# Revit family: Class-II-Fan_VBBB-CCW-TAD_Carnes
name_source: partatom
category: Mechanical Equipment
revit_build: Autodesk Revit Architecture 2012 (Build: 20110309_2315(x64)
units: mm (PartAtom-declared; Revit-internal decimal feet)

## types (12) — shared parameters
04 CSI = 23 34 23
95 CSI = 15830
Angle = 135.00°
Assembly Code = D3040200
Catalog URL = http://www.carnes.com
Description = Cetrifugal Blowers
Housing = Aluminum-Carnes-Spun-Brushed
IOM Instructions URL = http://www.carnes.com
Manufacturer = Carnes Company
Manufacturer Fax = 608-845-6470
Motor Cover = No
Product Page URL = http://www.carnes.com
URL = http://www.carnes.com
Warranty URL = http://www.carnes.com
Weather Cover = Yes
ecoScorecard Product Page = http://ecoscorecard.com
zero-valued in all types: Default Elevation

## per-type parameters (varying)
- VBBB-CCW-TAD 12: 001=21.6 "; A=13 "; B=9.8 "; C=13.3 "; D=17.6 "; DX=1 "; Drip=4.9 "; Drip1=4.9 "; G=16 "; H=32 "; HA=9.8 "; HC=13.9 "; HE=10.6 "; HG=9.3 "; HJ=9.3 "; HN=12.9 "; J=7.4 "; KL=2 "; Model=VBBB 12; Motor Pedastal Stand=18.6 "; P=26.5 "; Radius=6.6 "; SD=1.2 "; SD Radius=0.6 "; SE=2.8 "; Support Plate Drip=17.6 "; Weather Cover Height=22.4 "; Weather Cover Length=23.4 "; Weather Cover Width=13 "
- VBBB-CCW-TAD 13: 001=24.2 "; A=14.3 "; B=10.8 "; C=14.6 "; D=19.1 "; DX=1 "; Drip=7.4 "; Drip1=5.4 "; G=17.5 "; H=34.8 "; HA=10.8 "; HC=15.3 "; HE=11.6 "; HG=10.3 "; HJ=10.3 "; HN=14.3 "; J=8 "; KL=2.6 "; Model=VBBB 13; Motor Pedastal Stand=20.5 "; P=29.6 "; Radius=7.3 "; SD=1.2 "; SD Radius=0.6 "; SE=3.4 "; Support Plate Drip=15.8 "; Weather Cover Height=22.8 "; Weather Cover Length=25.4 "; Weather Cover Width=14.5 "
- VBBB-CCW-TAD 15: 001=24.2 "; A=15.9 "; B=11.9 "; C=16.2 "; D=19.4 "; DX=1 "; Drip=6.9 "; Drip1=6 "; G=19 "; H=36 "; HA=11.9 "; HC=16.8 "; HE=12.9 "; HG=11.4 "; HJ=11.4 "; HN=15.8 "; J=9.1 "; KL=2.6 "; Model=VBBB 15; Motor Pedastal Stand=20.5 "; P=30.1 "; Radius=8.1 "; SD=1.2 "; SD Radius=0.6 "; SE=3.4 "; Support Plate Drip=17.8 "; Weather Cover Height=25.5 "; Weather Cover Length=25.4 "; Weather Cover Width=16 "
- VBBB-CCW-TAD 16: 001=24.2 "; A=17.4 "; B=13.2 "; C=17.8 "; D=19.4 "; DX=1 "; Drip=6.9 "; Drip1=6.6 "; G=20.5 "; H=37.3 "; HA=13.1 "; HC=18.4 "; HE=14.1 "; HG=12.5 "; HJ=12.6 "; HN=17.4 "; J=9.7 "; KL=2.6 "; Model=VBBB 16; Motor Pedastal Stand=20.5 "; P=30.8 "; Radius=8.9 "; SD=1.2 "; SD Radius=0.6 "; SE=3.4 "; Support Plate Drip=19 "; Weather Cover Height=28 "; Weather Cover Length=25.4 "; Weather Cover Width=17.5 "
- VBBB-CCW-TAD 18: 001=29.5 "; A=19.4 "; B=14.6 "; C=19.5 "; D=21.9 "; DX=1.3 "; Drip=6.4 "; Drip1=7.3 "; G=22.5 "; H=43.4 "; HA=14.5 "; HC=20.6 "; HE=15.7 "; HG=13.8 "; HJ=14 "; HN=19.3 "; J=10.9 "; KL=3.3 "; Model=VBBB 18; Motor Pedastal Stand=25.3 "; P=36.8 "; Radius=9.8 "; SD=1.4 "; SD Radius=0.7 "; SE=4 "; Support Plate Drip=21 "; Weather Cover Height=32 "; Weather Cover Length=30.9 "; Weather Cover Width=19.5 "
- VBBB-CCW-TAD 20: 001=29.5 "; A=21.2 "; B=15.9 "; C=21.4 "; D=22.8 "; DX=1.3 "; Drip=6.4 "; Drip1=8 "; G=25 "; H=44.8 "; HA=15.8 "; HC=22.4 "; HE=17.3 "; HG=15.2 "; HJ=15.3 "; HN=21.1 "; J=11.6 "; KL=3.3 "; Model=VBBB 20; Motor Pedastal Stand=25.3 "; P=37.5 "; Radius=10.7 "; SD=1.4 "; SD Radius=0.7 "; SE=4 "; Support Plate Drip=22.8 "; Weather Cover Height=35 "; Weather Cover Length=30.9 "; Weather Cover Width=22 "
- VBBB-CCW-TAD 22: 001=29.5 "; A=23.6 "; B=17.7 "; C=23.8 "; D=25.5 "; DX=1.3 "; Drip=6.4 "; Drip1=8.8 "; G=27.3 "; H=47.1 "; HA=17.7 "; HC=24.8 "; HE=19.1 "; HG=16.8 "; HJ=17.2 "; HN=23.5 "; J=12.4 "; KL=3.3 "; Model=VBBB 22; Motor Pedastal Stand=25.3 "; P=38.4 "; Radius=11.9 "; SD=1.4 "; SD Radius=0.7 "; SE=4 "; Support Plate Drip=25.5 "; Weather Cover Height=32.3 "; Weather Cover Length=30.8 "; Weather Cover Width=24.3 "
- VBBB-CCW-TAD 24: 001=29.5 "; A=25.9 "; B=19.4 "; C=26.1 "; D=28 "; DX=1.3 "; Drip=6.4 "; Drip1=9.7 "; G=29.8 "; H=48.8 "; HA=19.5 "; HC=27.1 "; HE=21 "; HG=18.5 "; HJ=19 "; HN=25.9 "; J=13.3 "; KL=3.3 "; Model=VBBB 24; Motor Pedastal Stand=25.3 "; P=39.3 "; Radius=13 "; SD=1.7 "; SD Radius=0.8 "; SE=4 "; Support Plate Drip=28 "; Weather Cover Height=36.4 "; Weather Cover Length=30.8 "; Weather Cover Width=26.8 "
- VBBB-CCW-TAD 27: 001=32.4 "; A=28.6 "; B=21.4 "; C=28.5 "; D=30.5 "; DX=1.5 "; Drip=6.4 "; Drip1=10.7 "; G=33 "; H=53 "; HA=21.4 "; HC=30.1 "; HE=23.2 "; HG=20.4 "; HJ=20.9 "; HN=28.6 "; J=14.3 "; KL=3.6 "; Model=VBBB 27; Motor Pedastal Stand=27.6 "; P=43.1 "; Radius=14.3 "; SD=1.7 "; SD Radius=0.8 "; SE=4.6 "; Support Plate Drip=30.5 "; Weather Cover Height=40.8 "; Weather Cover Length=33.7 "; Weather Cover Width=30 "
- VBBB-CCW-TAD 30: 001=32.5 "; A=31.8 "; B=23.8 "; C=31.6 "; D=27.5 "; DX=1.5 "; Drip=6.4 "; Drip1=11.9 "; G=36.1 "; H=56 "; HA=23.8 "; HC=33.3 "; HE=25.8 "; HG=22.8 "; HJ=23.3 "; HN=31.8 "; J=15.5 "; KL=3.6 "; Model=VBBB 30; Motor Pedastal Stand=27.7 "; P=44.4 "; Radius=15.8 "; SD=1.9 "; SD Radius=1 "; SE=4.6 "; Support Plate Drip=27.5 "; Weather Cover Height=38 "; Weather Cover Length=33.8 "; Weather Cover Width=33.1 "
- VBBB-CCW-TAD 33: 001=36.7 "; A=35.1 "; B=26.1 "; C=34.8 "; D=30 "; DX=1.5 "; Drip=6.4 "; Drip1=13 "; G=38.9 "; H=61.8 "; HA=26.3 "; HC=36.6 "; HE=28.4 "; HG=25 "; HJ=25.8 "; HN=35.1 "; J=16.6 "; KL=4.5 "; Model=VBBB 33; Motor Pedastal Stand=31.2 "; P=49.7 "; Radius=17.4 "; SD=2.2 "; SD Radius=1.1 "; SE=5.3 "; Support Plate Drip=30 "; Weather Cover Height=40.5 "; Weather Cover Length=37.9 "; Weather Cover Width=35.9 "
- VBBB-CCW-TAD 36: 001=36.6 "; A=38.8 "; B=28.9 "; C=38.5 "; D=33.5 "; DX=1.5 "; Drip=6.5 "; Drip1=14.4 "; G=43.8 "; H=64.6 "; HA=29 "; HC=40.1 "; HE=31.5 "; HG=27.8 "; HJ=28.5 "; HN=39.6 "; J=18 "; KL=4.5 "; Model=VBBB 36; Motor Pedastal Stand=31.1 "; P=51.1 "; Radius=19.3 "; SD=2.4 "; SD Radius=1.2 "; SE=5.3 "; Support Plate Drip=33.5 "; Weather Cover Height=46.3 "; Weather Cover Length=38.2 "; Weather Cover Width=40.8 "

## geometry (parser evidence)
native form markers: Blend x2, Sweep x33
no freeform markers — native parametric forms only
